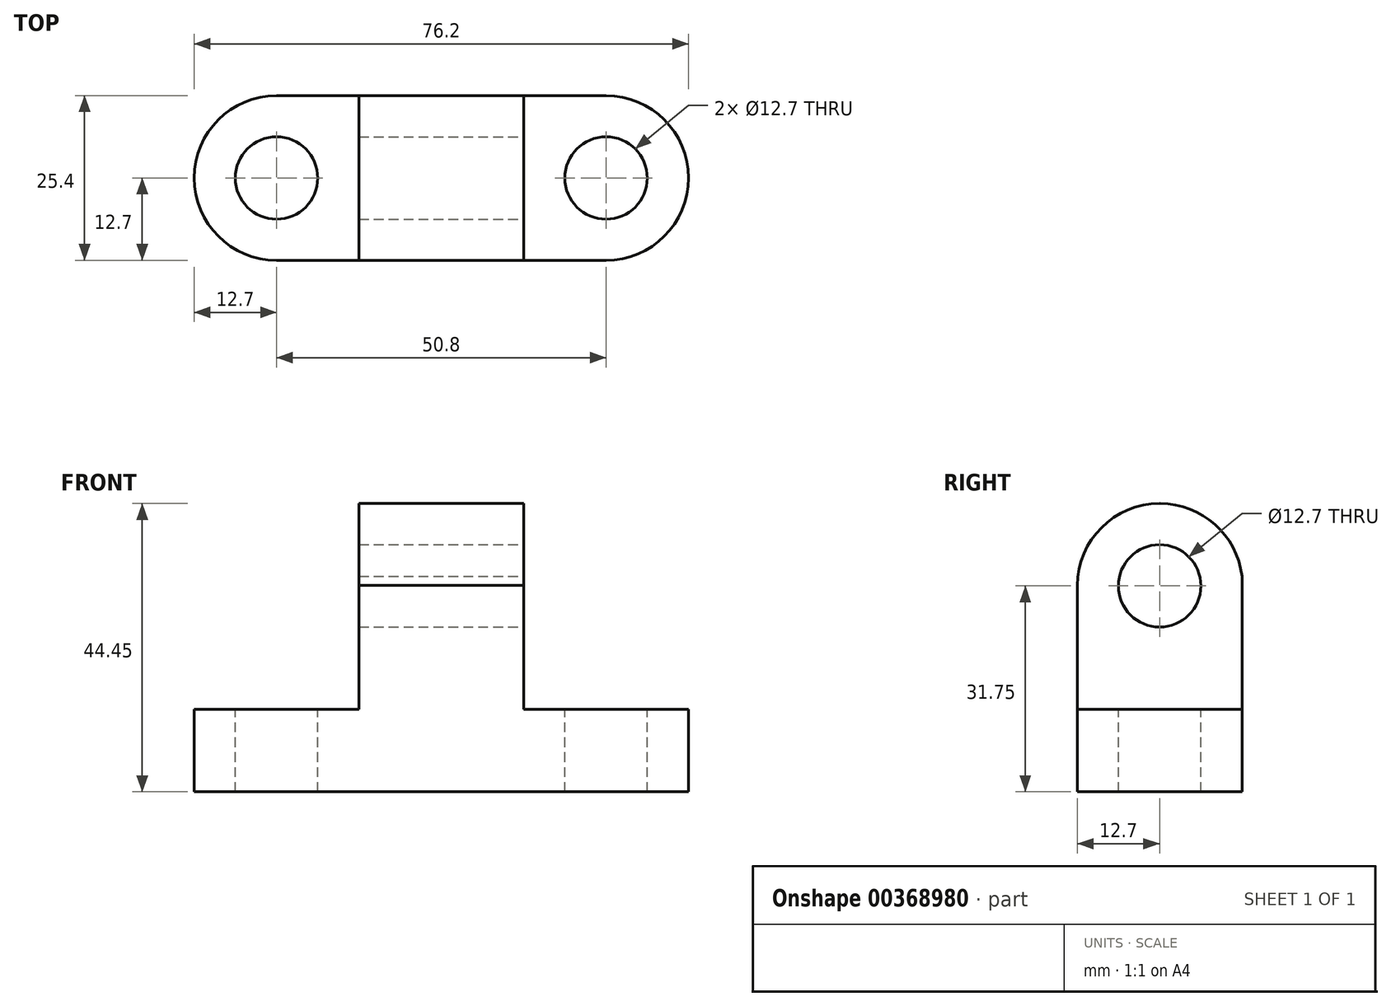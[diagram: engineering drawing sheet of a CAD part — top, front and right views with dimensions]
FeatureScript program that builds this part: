
annotation { "Feature Type Name" : "Feature", "Feature Type Description" : "" }
export const myFeature = defineFeature(function(context is Context, id is Id, definition is map)
    precondition{}
    {
        {
            var Q0;
            Q0=qCreatedBy(makeId("Front.planeOp"),FACE);
            var sketch = newSketch(context, id + "F0", { "sketchPlane" : qUnion([Q0])});
            skLineSegment(sketch, "E0", {"start": v(0, 0) * mm, "end": v(76.2, 0) * mm});
            skLineSegment(sketch, "E1", {"start": v(76.2, 0) * mm, "end": v(76.2, 12.7) * mm});
            skLineSegment(sketch, "E2", {"start": v(76.2, 12.7) * mm, "end": v(50.8, 12.7) * mm});
            skLineSegment(sketch, "E3", {"start": v(50.8, 12.7) * mm, "end": v(50.8, 44.45) * mm});
            skLineSegment(sketch, "E4", {"start": v(50.8, 44.45) * mm, "end": v(25.4, 44.45) * mm});
            skLineSegment(sketch, "E5", {"start": v(25.4, 44.45) * mm, "end": v(25.4, 12.7) * mm});
            skLineSegment(sketch, "E6", {"start": v(25.4, 12.7) * mm, "end": v(0, 12.7) * mm});
            skLineSegment(sketch, "E7", {"start": v(0, 12.7) * mm, "end": v(0, 0) * mm});
            skSolve(sketch);
        }
        {
            var Q0;
            Q0=makeQuery(id+"F0.imprint","IMPRINT",FACE,{"disambiguationData":[TD([[makeQuery(id+"F0.imprint","IMPRINT",EDGE,{"derivedFrom":sQuery(id+"F0.wireOp",EDGE,"E0")}),1.0]])]});
            extrude(context, id + "F1", {"entities" : qUnion([Q0]), "depth" : 25.4 * mm});
        }
        {
            var Q0;
            Q0=makeQuery(id+"F1.opExtrude","SWEPT_FACE",FACE,{"disambiguationData":[OSD([sQuery(id+"F0.wireOp",EDGE,"E3")])]});
            var sketch = newSketch(context, id + "F2", { "sketchPlane" : qUnion([Q0])});
            skCircle(sketch, "E8", {"center": v(-12.7, 31.75) * mm, "radius": 6.35 * mm});
            skCircle(sketch, "E9", {"center": v(-12.65, 31.7) * mm, "radius": 12.75 * mm});
            skPoint(sketch, "E9.first.point", {"position": v(-25.4, 31.84) * mm});
            skPoint(sketch, "E9.second.point", {"position": v(-12.7, 44.45) * mm});
            skPoint(sketch, "E9.third.point", {"position": v(0, 30.17) * mm});
            skSolve(sketch);
        }
        {
            var Q0;
            Q0=makeQuery(id+"F2.imprint","IMPRINT",FACE,{"disambiguationData":[TD([[makeQuery(id+"F2.imprint","IMPRINT",EDGE,{"derivedFrom":sQuery(id+"F2.wireOp",EDGE,"E8")}),1.0]])]});
            var Q1;
            {var subQ0=sQuery(id+"F2.wireOp",EDGE,"E9");var subQ1=sQuery(id+"F0.wireOp",EDGE,"E3");var subQ2=makeQuery(id+"F1.opExtrude","SWEPT_EDGE",EDGE,{"disambiguationData":[OSD([subQ1,sQuery(id+"F0.wireOp",EDGE,"E4")])]});var subQ3=makeQuery(id+"F2.imprint","INTERSECT",VERTEX,{"disambiguationData":[OD(1.0)],"derivedFrom":[subQ2,subQ0]});var subQ4=makeQuery(id+"F1.opExtrude","CAP_EDGE",EDGE,{"disambiguationData":[OSD([subQ1])],"isStart":false});var subQ5=makeQuery(id+"F2.imprint","INTERSECT",VERTEX,{"disambiguationData":[OD(0.0)],"derivedFrom":[subQ4,subQ0]});Q1=makeQuery(id+"F2.imprint","IMPRINT",FACE,{"disambiguationData":[TD([[makeQuery(id+"F2.imprint","IMPRINT",EDGE,{"disambiguationData":[TD([[subQ3,-1.0],[subQ5,1.0]])],"derivedFrom":subQ0}),-1.0]])]});}
            var Q2;
            {var subQ0=sQuery(id+"F2.wireOp",EDGE,"E9");var subQ1=sQuery(id+"F0.wireOp",EDGE,"E3");var subQ2=makeQuery(id+"F1.opExtrude","SWEPT_EDGE",EDGE,{"disambiguationData":[OSD([subQ1,sQuery(id+"F0.wireOp",EDGE,"E4")])]});var subQ3=makeQuery(id+"F2.imprint","INTERSECT",VERTEX,{"disambiguationData":[OD(0.0)],"derivedFrom":[subQ2,subQ0]});var subQ4=makeQuery(id+"F1.opExtrude","CAP_EDGE",EDGE,{"disambiguationData":[OSD([subQ1])],"isStart":true});var subQ5=makeQuery(id+"F2.imprint","INTERSECT",VERTEX,{"disambiguationData":[OD(0.0)],"derivedFrom":[subQ4,subQ0]});Q2=makeQuery(id+"F2.imprint","IMPRINT",FACE,{"disambiguationData":[TD([[makeQuery(id+"F2.imprint","IMPRINT",EDGE,{"disambiguationData":[TD([[subQ3,1.0],[subQ5,-1.0]])],"derivedFrom":subQ0}),-1.0]])]});}
            extrude(context, id + "F3", {"entities" : qUnion([Q0, Q1, Q2]), "operationType" : NewBodyOperationType.REMOVE, "oppositeDirection" : true, "depth" : 25.4 * mm});
        }
        {
            var Q0;
            Q0=makeQuery(id+"F1.opExtrude","SWEPT_FACE",FACE,{"disambiguationData":[OSD([sQuery(id+"F0.wireOp",EDGE,"E6")])]});
            var sketch = newSketch(context, id + "F4", { "sketchPlane" : qUnion([Q0])});
            skCircle(sketch, "E10", {"center": v(12.7, -12.7) * mm, "radius": 6.35 * mm});
            skCircle(sketch, "E11", {"center": v(63.5, -12.7) * mm, "radius": 6.35 * mm});
            skCircle(sketch, "E12", {"center": v(12.7, -12.7) * mm, "radius": 12.7 * mm});
            skPoint(sketch, "E12.first.point", {"position": v(0, -12.7) * mm});
            skPoint(sketch, "E12.second.point", {"position": v(12.7, 0) * mm});
            skPoint(sketch, "E12.third.point", {"position": v(25.4, -12.7) * mm});
            skPoint(sketch, "E13.first.point", {"position": v(63.76, 0) * mm});
            skPoint(sketch, "E13.second.point", {"position": v(63.5, -25.85) * mm});
            skPoint(sketch, "E13.third.point", {"position": v(74.55, -19.95) * mm});
            skCircle(sketch, "E14", {"center": v(63.25, -12.92) * mm, "radius": 12.93 * mm});
            skPoint(sketch, "E14.second.point", {"position": v(76.18, -12.7) * mm});
            skSolve(sketch);
        }
        {
            var Q0;
            Q0=makeQuery(id+"F4.imprint","IMPRINT",FACE,{"disambiguationData":[TD([[makeQuery(id+"F4.imprint","IMPRINT",EDGE,{"derivedFrom":sQuery(id+"F4.wireOp",EDGE,"E10")}),1.0]])]});
            var Q1;
            {var subQ0=sQuery(id+"F4.wireOp",EDGE,"E12");var subQ1=sQuery(id+"F0.wireOp",EDGE,"E6");var subQ2=makeQuery(id+"F1.opExtrude","CAP_EDGE",EDGE,{"disambiguationData":[OSD([subQ1])],"isStart":true});var subQ3=makeQuery(id+"F4.imprint","INTERSECT",VERTEX,{"derivedFrom":[subQ2,subQ0]});Q1=makeQuery(id+"F4.imprint","IMPRINT",FACE,{"disambiguationData":[TD([[makeQuery(id+"F4.imprint","IMPRINT",EDGE,{"disambiguationData":[TD([[subQ3,-1.0]])],"derivedFrom":subQ0}),-1.0]])]});}
            var Q2;
            Q2=makeQuery(id+"F4.imprint","IMPRINT",FACE,{"disambiguationData":[TD([[makeQuery(id+"F4.imprint","IMPRINT",EDGE,{"derivedFrom":sQuery(id+"F4.wireOp",EDGE,"E11")}),1.0]])]});
            var Q3;
            {var subQ0=sQuery(id+"F4.wireOp",EDGE,"E12");var subQ1=sQuery(id+"F0.wireOp",EDGE,"E6");var subQ4=makeQuery(id+"F1.opExtrude","CAP_EDGE",EDGE,{"disambiguationData":[OSD([subQ1])],"isStart":false});var subQ5=makeQuery(id+"F4.imprint","INTERSECT",VERTEX,{"derivedFrom":[subQ4,subQ0]});Q3=makeQuery(id+"F4.imprint","IMPRINT",FACE,{"disambiguationData":[TD([[makeQuery(id+"F4.imprint","IMPRINT",EDGE,{"disambiguationData":[TD([[subQ5,1.0]])],"derivedFrom":subQ0}),-1.0]])]});}
            extrude(context, id + "F5", {"entities" : qUnion([Q0, Q1, Q2, Q3]), "operationType" : NewBodyOperationType.REMOVE, "oppositeDirection" : true, "depth" : 12.7 * mm});
        }
        {
            var Q0;
            Q0=makeQuery(id+"F1.opExtrude","SWEPT_FACE",FACE,{"disambiguationData":[OSD([sQuery(id+"F0.wireOp",EDGE,"E2")])]});
            var sketch = newSketch(context, id + "F6", { "sketchPlane" : qUnion([Q0])});
            skArc(sketch, "E15", {"start": v(63.5, -25.4) * mm, "mid": v(76.2, -12.7) * mm, "end": v(63.5, 0) * mm});
            skSolve(sketch);
        }
        {
            var Q0;
            {var subQ0=sQuery(id+"F6.wireOp",EDGE,"E15");Q0=makeQuery(id+"F6.imprint","IMPRINT",FACE,{"disambiguationData":[TD([[makeQuery(id+"F6.imprint","IMPRINT",EDGE,{"derivedFrom":subQ0}),-1.0]])]});}
            extrude(context, id + "F7", {"entities" : qUnion([Q0]), "operationType" : NewBodyOperationType.REMOVE, "oppositeDirection" : true, "depth" : 12.7 * mm});
        }
    });
